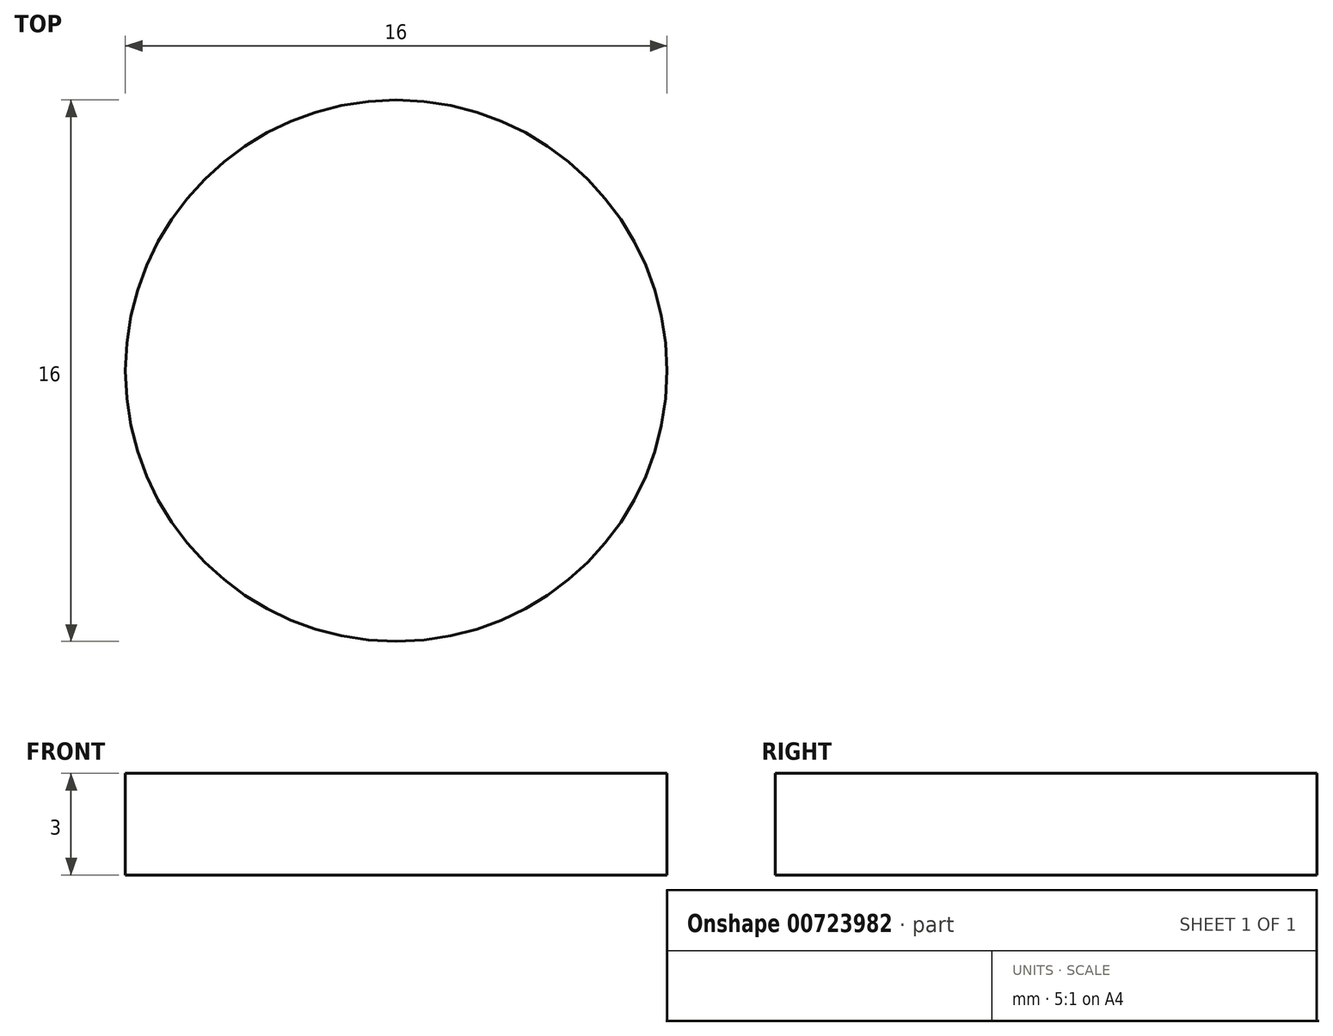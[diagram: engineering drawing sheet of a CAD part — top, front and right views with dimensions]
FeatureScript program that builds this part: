
annotation { "Feature Type Name" : "Feature", "Feature Type Description" : "" }
export const myFeature = defineFeature(function(context is Context, id is Id, definition is map)
    precondition{}
    {
        {
            var Q0;
            Q0=qCreatedBy(makeId("Top.planeOp"),FACE);
            var sketch = newSketch(context, id + "F0", { "sketchPlane" : qUnion([Q0])});
            skCircle(sketch, "E0", {"center": v(0, 0) * mm, "radius": 8 * mm});
            skSolve(sketch);
        }
        {
            var Q0;
            Q0=qSketchRegion(id+"F0",true);
            extrude(context, id + "F1", {"entities" : qUnion([Q0]), "depth" : 3 * mm, "offsetDistance" : 25 * mm});
        }
    });
